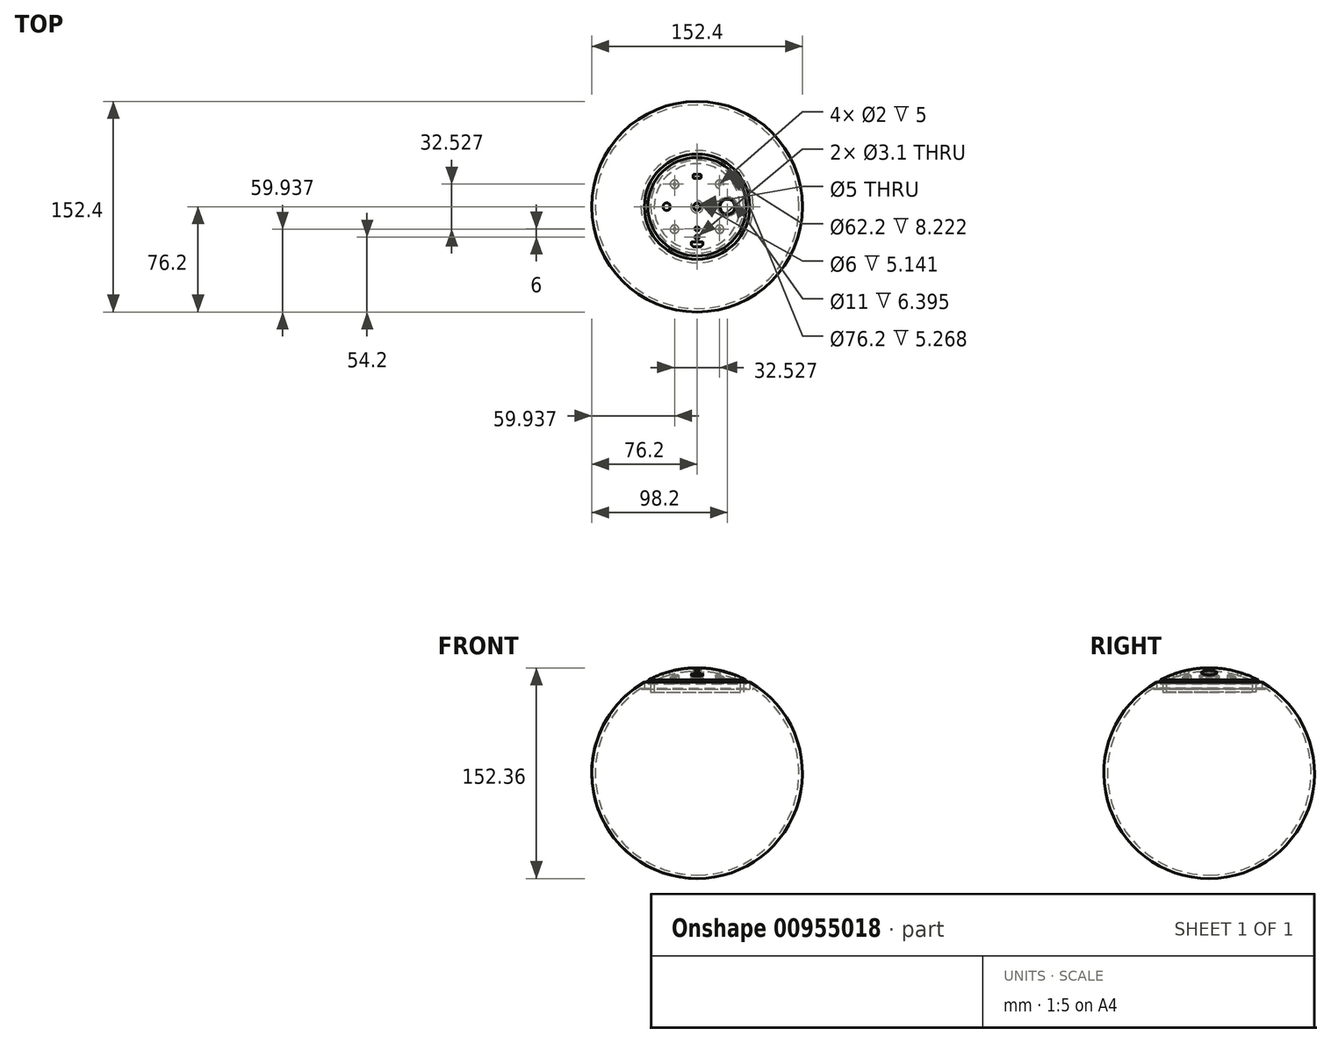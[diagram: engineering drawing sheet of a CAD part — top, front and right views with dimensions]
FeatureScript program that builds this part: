
annotation { "Feature Type Name" : "Feature", "Feature Type Description" : "" }
export const myFeature = defineFeature(function(context is Context, id is Id, definition is map)
    precondition{}
    {
        {
            var Q0;
            Q0=qCreatedBy(makeId("Front.planeOp"),FACE);
            var sketch = newSketch(context, id + "F0", { "sketchPlane" : qUnion([Q0])});
            skArc(sketch, "E0", {"start": v(-38.1, 66) * mm, "mid": v(-73.6, -19.72) * mm, "end": v(0, -76.2) * mm});
            skLineSegment(sketch, "E1", {"start": v(0, 0) * mm, "end": v(0, 126.02) * mm, "construction": true});
            skLineSegment(sketch, "E2.0", {"start": v(38.1, 0) * mm, "end": v(38.1, 126.02) * mm, "construction": true});
            skLineSegment(sketch, "E3.0", {"start": v(-38.1, 0) * mm, "end": v(-38.1, 126.02) * mm, "construction": true});
            skLineSegment(sketch, "E4", {"start": v(0, 0) * mm, "end": v(0, -76.2) * mm, "construction": true});
            skLineSegment(sketch, "E5", {"start": v(0, -76.2) * mm, "end": v(0, -73.7) * mm});
            skLineSegment(sketch, "E6.0", {"start": v(-40.6, 0) * mm, "end": v(-40.6, 61.5) * mm});
            skLineSegment(sketch, "E7", {"start": v(-40.6, 60.72) * mm, "end": v(-38.1, 60.72) * mm});
            skLineSegment(sketch, "E8", {"start": v(-38.1, 60.72) * mm, "end": v(-38.1, 66) * mm});
            skArc(sketch, "E9.trimOffspring", {"start": v(-40.6, 61.5) * mm, "mid": v(-70.59, -21.2) * mm, "end": v(0, -73.7) * mm});
            skSolve(sketch);
        }
        {
            var Q0;
            {var subQ5=sQuery(id+"F0.wireOp",EDGE,"E0");Q0=makeQuery(id+"F0.imprint","IMPRINT",FACE,{"disambiguationData":[TD([[makeQuery(id+"F0.imprint","IMPRINT",EDGE,{"derivedFrom":subQ5}),1.0]])]});}
            var Q1;
            Q1=sQuery(id+"F0.wireOp",EDGE,"E1");
            revolve(context, id + "F1", {"surfaceOperationType" : NewSurfaceOperationType.NEW, "entities" : qUnion([Q0]), "axis" : qUnion([Q1]), "revolveType" : RevolveType.FULL});
        }
        {
            var Q0;
            Q0=qCreatedBy(makeId("Front.planeOp"),FACE);
            var sketch = newSketch(context, id + "F2", { "sketchPlane" : qUnion([Q0])});
            skArc(sketch, "E10", {"start": v(0, 76.2) * mm, "mid": v(-18.34, 73.96) * mm, "end": v(-35.6, 67.37) * mm});
            skLineSegment(sketch, "E11", {"start": v(0, 0) * mm, "end": v(0, 119.66) * mm, "construction": true});
            skLineSegment(sketch, "E12.0", {"start": v(-38.1, 0) * mm, "end": v(-38.1, 119.66) * mm, "construction": true});
            skArc(sketch, "E13.0", {"start": v(0, 73.7) * mm, "mid": v(-15.93, 71.96) * mm, "end": v(-31.1, 66.82) * mm});
            skLineSegment(sketch, "E14.0", {"start": v(-35.6, 64.53) * mm, "end": v(-35.6, 67.37) * mm});
            skLineSegment(sketch, "E15.0", {"start": v(-33.6, 58.6) * mm, "end": v(-33.6, 65.6) * mm});
            skLineSegment(sketch, "E16.0", {"start": v(-31.1, 58.6) * mm, "end": v(-31.1, 66.82) * mm});
            skArc(sketch, "E17.trimOffspring", {"start": v(-33.6, 65.6) * mm, "mid": v(-34.6, 65.07) * mm, "end": v(-35.6, 64.53) * mm});
            skLineSegment(sketch, "E18", {"start": v(-33.6, 58.6) * mm, "end": v(-31.1, 58.6) * mm});
            skLineSegment(sketch, "E19", {"start": v(0, 76.2) * mm, "end": v(0, 73.7) * mm});
            skSolve(sketch);
        }
        {
            var Q0;
            Q0 = qSketchRegion(id + "F2", true);
            var Q1;
            Q1=sQuery(id+"F2.wireOp",EDGE,"E11");
            revolve(context, id + "F3", {"surfaceOperationType" : NewSurfaceOperationType.NEW, "entities" : qUnion([Q0]), "axis" : qUnion([Q1]), "revolveType" : RevolveType.FULL});
        }
        {
            var Q0;
            Q0=qCreatedBy(makeId("Top.planeOp"),FACE);
            cPlane(context, id + "F4", {"entities" : qUnion([Q0]), "cplaneType" : CPlaneType.OFFSET, "offset" : 81.28 * mm, "width" : 152.4 * mm, "height" : 152.4 * mm});
        }
        {
            var Q0;
            Q0=qCreatedBy(id+"F4.planeOp",FACE);
            var sketch = newSketch(context, id + "F5", { "sketchPlane" : qUnion([Q0])});
            skLineSegment(sketch, "E20.bottom", {"start": v(3.7, -25.5) * mm, "end": v(-3.7, -25.5) * mm});
            skLineSegment(sketch, "E20.top", {"start": v(4.2, -27.6) * mm, "end": v(-4.2, -27.6) * mm});
            skLineSegment(sketch, "E20.left", {"start": v(4.2, -26) * mm, "end": v(4.2, -27.42) * mm});
            skLineSegment(sketch, "E20.right", {"start": v(-4.2, -26) * mm, "end": v(-4.2, -27.42) * mm});
            skPoint(sketch, "E20.middle", {"position": v(0, -26.55) * mm});
            skLineSegment(sketch, "E21.0", {"start": v(1.38, -28.9) * mm, "end": v(-1.07, -28.9) * mm, "construction": true});
            skLineSegment(sketch, "E22.0", {"start": v(2.7, -21.08) * mm, "end": v(2.7, -25.34) * mm, "construction": true});
            skLineSegment(sketch, "E23.0", {"start": v(-2.7, -21.08) * mm, "end": v(-2.7, -25.34) * mm, "construction": true});
            skLineSegment(sketch, "E24", {"start": v(-4.06, -27.72) * mm, "end": v(-2.81, -28.8) * mm});
            skLineSegment(sketch, "E25", {"start": v(2.81, -28.8) * mm, "end": v(4.06, -27.72) * mm});
            skLineSegment(sketch, "E26", {"start": v(-2.55, -28.9) * mm, "end": v(2.55, -28.9) * mm});
            skPoint(sketch, "E27.visualSharp", {"position": v(-4.2, -25.5) * mm});
            skArc(sketch, "E27.filletArc", {"start": v(-3.7, -25.5) * mm, "mid": v(-4.05, -25.65) * mm, "end": v(-4.2, -26) * mm});
            skPoint(sketch, "E28.visualSharp", {"position": v(4.2, -25.5) * mm});
            skArc(sketch, "E28.filletArc", {"start": v(4.2, -26) * mm, "mid": v(4.05, -25.65) * mm, "end": v(3.7, -25.5) * mm});
            skPoint(sketch, "E29.visualSharp", {"position": v(4.2, -27.6) * mm});
            skArc(sketch, "E29.filletArc", {"start": v(4.06, -27.72) * mm, "mid": v(4.16, -27.58) * mm, "end": v(4.2, -27.42) * mm});
            skPoint(sketch, "E30.visualSharp", {"position": v(2.7, -28.9) * mm});
            skArc(sketch, "E30.filletArc", {"start": v(2.55, -28.9) * mm, "mid": v(2.7, -28.87) * mm, "end": v(2.81, -28.8) * mm});
            skPoint(sketch, "E31.visualSharp", {"position": v(-2.7, -28.9) * mm});
            skArc(sketch, "E31.filletArc", {"start": v(-2.81, -28.8) * mm, "mid": v(-2.7, -28.87) * mm, "end": v(-2.55, -28.9) * mm});
            skPoint(sketch, "E32.visualSharp", {"position": v(-4.2, -27.6) * mm});
            skArc(sketch, "E32.filletArc", {"start": v(-4.2, -27.42) * mm, "mid": v(-4.16, -27.58) * mm, "end": v(-4.06, -27.72) * mm});
            skSolve(sketch);
        }
        {
            var Q0;
            Q0=qCreatedBy(id+"F4.planeOp",FACE);
            var sketch = newSketch(context, id + "F6", { "sketchPlane" : qUnion([Q0])});
            skCircle(sketch, "E33", {"center": v(0, 0) * mm, "radius": 22 * mm, "construction": true});
            skCircle(sketch, "E34", {"center": v(0, -22) * mm, "radius": 1.55 * mm});
            skLineSegment(sketch, "E35", {"start": v(0, 0) * mm, "end": v(0, -21.23) * mm, "construction": true});
            skCircle(sketch, "E36.0.1.0", {"center": v(0, -16) * mm, "radius": 1.55 * mm});
            skLineSegment(sketch, "E36.direction1", {"start": v(0, -22) * mm, "end": v(25, -22) * mm, "construction": true});
            skLineSegment(sketch, "E36.direction2", {"start": v(0, -22) * mm, "end": v(0, -16) * mm, "construction": true});
            skSolve(sketch);
        }
        {
            var Q0;
            Q0=qCreatedBy(id+"F4.planeOp",FACE);
            var sketch = newSketch(context, id + "F7", { "sketchPlane" : qUnion([Q0])});
            skCircle(sketch, "E37", {"center": v(0, 0) * mm, "radius": 22 * mm, "construction": true});
            skCircle(sketch, "E38", {"center": v(22, 0) * mm, "radius": 5.5 * mm});
            skLineSegment(sketch, "E39.bottom", {"start": v(2.8, 23.4) * mm, "end": v(-2.8, 23.4) * mm});
            skLineSegment(sketch, "E39.top", {"start": v(2.8, 20.6) * mm, "end": v(-2.8, 20.6) * mm});
            skLineSegment(sketch, "E39.left", {"start": v(2.8, 23.4) * mm, "end": v(2.8, 20.6) * mm});
            skLineSegment(sketch, "E39.right", {"start": v(-2.8, 23.4) * mm, "end": v(-2.8, 20.6) * mm});
            skPoint(sketch, "E39.middle", {"position": v(0, 22) * mm});
            skSolve(sketch);
        }
        {
            var Q0;
            Q0=qCreatedBy(id+"F4.planeOp",FACE);
            var sketch = newSketch(context, id + "F8", { "sketchPlane" : qUnion([Q0])});
            skCircle(sketch, "E40", {"center": v(0, 0) * mm, "radius": 22 * mm, "construction": true});
            skArc(sketch, "E41", {"start": v(-24.4, -1.24) * mm, "mid": v(-22, -2.7) * mm, "end": v(-19.6, -1.24) * mm});
            skLineSegment(sketch, "E42", {"start": v(-22, 0) * mm, "end": v(-22, 4.73) * mm, "construction": true});
            skLineSegment(sketch, "E43.0", {"start": v(-24.4, -2.74) * mm, "end": v(-24.4, 4.73) * mm});
            skLineSegment(sketch, "E44.MirrorCS", {"start": v(-19.6, -2.74) * mm, "end": v(-19.6, 4.73) * mm});
            skArc(sketch, "E45.trimOffspring", {"start": v(-19.6, 1.24) * mm, "mid": v(-22, 2.7) * mm, "end": v(-24.4, 1.24) * mm});
            skSolve(sketch);
        }
        {
            var Q0;
            Q0=qCreatedBy(id+"F4.planeOp",FACE);
            var sketch = newSketch(context, id + "F9", { "sketchPlane" : qUnion([Q0])});
            skCircle(sketch, "E46", {"center": v(0, 0) * mm, "radius": 2.5 * mm});
            skSolve(sketch);
        }
        {
            var Q0;
            Q0 = qSketchRegion(id + "F9", true);
            extrude(context, id + "F10", {"entities" : qUnion([Q0]), "operationType" : NewBodyOperationType.REMOVE, "oppositeDirection" : true, "depth" : 25 * mm, "offsetDistance" : 25 * mm});
        }
        {
            var Q0;
            Q0=qCreatedBy(makeId("Top.planeOp"),FACE);
            cPlane(context, id + "F11", {"entities" : qUnion([Q0]), "cplaneType" : CPlaneType.OFFSET, "offset" : 70 * mm, "width" : 150 * mm, "height" : 150 * mm});
        }
        {
            var Q0;
            Q0=qCreatedBy(id+"F11.planeOp",FACE);
            var sketch = newSketch(context, id + "F12", { "sketchPlane" : qUnion([Q0])});
            skCircle(sketch, "E47", {"center": v(0, 0) * mm, "radius": 3 * mm});
            skSolve(sketch);
        }
        {
            var Q0;
            Q0 = qSketchRegion(id + "F12", true);
            var Q1;
            Q1=makeQuery(id+"F3.opRevolve","SWEPT_FACE",FACE,{"disambiguationData":[OSD([sQuery(id+"F2.wireOp",EDGE,"E10")])]});
            extrude(context, id + "F13", {"entities" : qUnion([Q0]), "operationType" : NewBodyOperationType.REMOVE, "endBound" : BoundingType.UP_TO_SURFACE, "depth" : 25 * mm, "endBoundEntityFace" : qUnion([Q1]), "hasOffset" : true, "offsetDistance" : 1 * mm});
        }
        {
            var Q0;
            Q0 = qSketchRegion(id + "F5", true);
            extrude(context, id + "F14", {"entities" : qUnion([Q0]), "operationType" : NewBodyOperationType.REMOVE, "oppositeDirection" : true, "depth" : 25.4 * mm, "offsetDistance" : 25.4 * mm});
        }
        {
            var Q0;
            Q0 = qSketchRegion(id + "F6", true);
            var Q1;
            Q1 = qSketchRegion(id + "F8", true);
            extrude(context, id + "F15", {"entities" : qUnion([Q0, Q1]), "operationType" : NewBodyOperationType.REMOVE, "oppositeDirection" : true, "depth" : 25 * mm, "offsetDistance" : 25 * mm});
        }
        {
            var Q0;
            Q0 = qSketchRegion(id + "F7", true);
            extrude(context, id + "F16", {"entities" : qUnion([Q0]), "operationType" : NewBodyOperationType.REMOVE, "oppositeDirection" : true, "depth" : 25 * mm, "offsetDistance" : 25 * mm});
        }
        {
            var Q0;
            Q0=qCreatedBy(makeId("Top.planeOp"),FACE);
            cPlane(context, id + "F17", {"entities" : qUnion([Q0]), "cplaneType" : CPlaneType.OFFSET, "offset" : 65 * mm, "width" : 150 * mm, "height" : 150 * mm});
        }
        {
            var Q0;
            Q0=qCreatedBy(id+"F17.planeOp",FACE);
            var sketch = newSketch(context, id + "F18", { "sketchPlane" : qUnion([Q0])});
            skCircle(sketch, "E48", {"center": v(-16.26, 16.26) * mm, "radius": 3 * mm});
            skLineSegment(sketch, "E49", {"start": v(0, 0) * mm, "end": v(-28.69, 28.69) * mm, "construction": true});
            skLineSegment(sketch, "E50", {"start": v(0, 0) * mm, "end": v(16.68, 16.68) * mm, "construction": true});
            skCircle(sketch, "E51.1.0", {"center": v(-16.26, -16.26) * mm, "radius": 3 * mm});
            skCircle(sketch, "E51.2.0", {"center": v(16.26, -16.26) * mm, "radius": 3 * mm});
            skCircle(sketch, "E51.3.0", {"center": v(16.26, 16.26) * mm, "radius": 3 * mm});
            skPoint(sketch, "E51.center", {"position": v(0, 0) * mm});
            skSolve(sketch);
        }
        {
            var Q0;
            Q0 = qSketchRegion(id + "F18", true);
            var Q1;
            Q1=makeQuery(id+"F3.opRevolve","SWEPT_FACE",FACE,{"disambiguationData":[OSD([sQuery(id+"F2.wireOp",EDGE,"E13.0")])]});
            extrude(context, id + "F19", {"entities" : qUnion([Q0]), "operationType" : NewBodyOperationType.ADD, "endBound" : BoundingType.UP_TO_SURFACE, "depth" : 25 * mm, "endBoundEntityFace" : qUnion([Q1]), "offsetDistance" : 25 * mm});
        }
        {
            var Q0;
            Q0=qCreatedBy(id+"F17.planeOp",FACE);
            var sketch = newSketch(context, id + "F20", { "sketchPlane" : qUnion([Q0])});
            skCircle(sketch, "E52.0", {"center": v(-16.26, 16.26) * mm, "radius": 3 * mm, "construction": true});
            skCircle(sketch, "E53", {"center": v(-16.26, 16.26) * mm, "radius": 1 * mm});
            skCircle(sketch, "E54.1.0", {"center": v(-16.26, -16.26) * mm, "radius": 1 * mm});
            skCircle(sketch, "E54.2.0", {"center": v(16.26, -16.26) * mm, "radius": 1 * mm});
            skCircle(sketch, "E54.3.0", {"center": v(16.26, 16.26) * mm, "radius": 1 * mm});
            skPoint(sketch, "E54.center", {"position": v(0, 0) * mm});
            skSolve(sketch);
        }
        {
            var Q0;
            Q0 = qSketchRegion(id + "F20", true);
            extrude(context, id + "F21", {"entities" : qUnion([Q0]), "operationType" : NewBodyOperationType.REMOVE, "depth" : 5 * mm, "offsetDistance" : 25 * mm});
        }
        {
            var Q0;
            Q0=qCreatedBy(makeId("Top.planeOp"),FACE);
            cPlane(context, id + "F22", {"entities" : qUnion([Q0]), "cplaneType" : CPlaneType.OFFSET, "offset" : 68 * mm, "width" : 150 * mm, "height" : 150 * mm});
        }
        {
            var Q0;
            Q0=qCreatedBy(id+"F22.planeOp",FACE);
            var sketch = newSketch(context, id + "F23", { "sketchPlane" : qUnion([Q0])});
            skCircle(sketch, "E55.0", {"center": v(22, 0) * mm, "radius": 5.5 * mm});
            skCircle(sketch, "E56.0", {"center": v(22, 0) * mm, "radius": 7 * mm});
            skSolve(sketch);
        }
        {
            var Q0;
            Q0 = qSketchRegion(id + "F23", true);
            var Q1;
            Q1=makeQuery(id+"F3.opRevolve","SWEPT_FACE",FACE,{"disambiguationData":[OSD([sQuery(id+"F2.wireOp",EDGE,"E13.0")])]});
            extrude(context, id + "F24", {"entities" : qUnion([Q0]), "operationType" : NewBodyOperationType.ADD, "endBound" : BoundingType.UP_TO_SURFACE, "depth" : 25 * mm, "endBoundEntityFace" : qUnion([Q1]), "offsetDistance" : 25 * mm});
        }
        {
            var Q0;
            Q0=qCreatedBy(id+"F22.planeOp",FACE);
            var sketch = newSketch(context, id + "F25", { "sketchPlane" : qUnion([Q0])});
            skCircle(sketch, "E57.0", {"center": v(22, 0) * mm, "radius": 5.5 * mm, "construction": true});
            skCircle(sketch, "E58.0", {"center": v(22, 0) * mm, "radius": 5.45 * mm});
            skSolve(sketch);
        }
        {
            var Q0;
            Q0 = qSketchRegion(id + "F25", true);
            var Q1;
            Q1=makeQuery(id+"F3.opRevolve","SWEPT_FACE",FACE,{"disambiguationData":[OSD([sQuery(id+"F2.wireOp",EDGE,"E10")])]});
            extrude(context, id + "F26", {"entities" : qUnion([Q0]), "endBound" : BoundingType.UP_TO_SURFACE, "depth" : 25 * mm, "endBoundEntityFace" : qUnion([Q1]), "offsetDistance" : 25 * mm});
        }
        {
            var Q0;
            Q0=makeQuery(id+"F26.opExtrude","CAP_FACE",FACE,{"disambiguationData":[OSD([sQuery(id+"F25.wireOp",EDGE,"E58.0")])],"isStart":true});
            var sketch = newSketch(context, id + "F27", { "sketchPlane" : qUnion([Q0])});
            skCircle(sketch, "E59", {"center": v(22, 0) * mm, "radius": 6.5 * mm});
            skSolve(sketch);
        }
        {
            var Q0;
            Q0 = qSketchRegion(id + "F27", true);
            extrude(context, id + "F28", {"entities" : qUnion([Q0]), "operationType" : NewBodyOperationType.ADD, "depth" : 1 * mm, "offsetDistance" : 25 * mm});
        }
        {
            var Q0;
            Q0=qCreatedBy(id+"F11.planeOp",FACE);
            var sketch = newSketch(context, id + "F29", { "sketchPlane" : qUnion([Q0])});
            skCircle(sketch, "E60.0", {"center": v(0, 0) * mm, "radius": 3 * mm});
            skCircle(sketch, "E61.0", {"center": v(0, 0) * mm, "radius": 4.5 * mm});
            skSolve(sketch);
        }
        {
            var Q0;
            Q0 = qSketchRegion(id + "F29", true);
            var Q1;
            Q1=makeQuery(id+"F3.opRevolve","SWEPT_FACE",FACE,{"disambiguationData":[OSD([sQuery(id+"F2.wireOp",EDGE,"E13.0")])]});
            extrude(context, id + "F30", {"entities" : qUnion([Q0]), "operationType" : NewBodyOperationType.ADD, "endBound" : BoundingType.UP_TO_SURFACE, "depth" : 25 * mm, "endBoundEntityFace" : qUnion([Q1]), "offsetDistance" : 25 * mm});
        }
        {
            var Q0;
            Q0=makeQuery(id+"F16.boolean.opBoolean","COPY",EDGE,{"derivedFrom":makeQuery(id+"F16.opExtrude","SWEPT_EDGE",EDGE,{"disambiguationData":[OSD([sQuery(id+"F7.wireOp",EDGE,"E39.bottom"),sQuery(id+"F7.wireOp",EDGE,"E39.right")])]})});
            var Q1;
            Q1=makeQuery(id+"F16.boolean.opBoolean","COPY",EDGE,{"derivedFrom":makeQuery(id+"F16.opExtrude","SWEPT_EDGE",EDGE,{"disambiguationData":[OSD([sQuery(id+"F7.wireOp",EDGE,"E39.top"),sQuery(id+"F7.wireOp",EDGE,"E39.right")])]})});
            var Q2;
            Q2=makeQuery(id+"F16.boolean.opBoolean","COPY",EDGE,{"derivedFrom":makeQuery(id+"F16.opExtrude","SWEPT_EDGE",EDGE,{"disambiguationData":[OSD([sQuery(id+"F7.wireOp",EDGE,"E39.top"),sQuery(id+"F7.wireOp",EDGE,"E39.left")])]})});
            var Q3;
            Q3=makeQuery(id+"F16.boolean.opBoolean","COPY",EDGE,{"derivedFrom":makeQuery(id+"F16.opExtrude","SWEPT_EDGE",EDGE,{"disambiguationData":[OSD([sQuery(id+"F7.wireOp",EDGE,"E39.bottom"),sQuery(id+"F7.wireOp",EDGE,"E39.left")])]})});
            fillet(context, id + "F31", {"entities" : qUnion([Q0, Q1, Q2, Q3]), "radius" : .5 * mm, "tangentPropagation" : true, "allowEdgeOverflow" : false});
        }
    });
